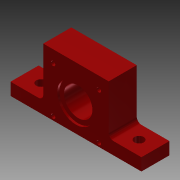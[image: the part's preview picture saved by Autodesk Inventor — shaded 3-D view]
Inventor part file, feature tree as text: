
AUTODESK INVENTOR PART (.ipt)
format: ipt  version: 2014 (Build 180170000, 170)  size: 166,400 bytes
history: native  units: in
note: dims shown in document units (in); Inventor stores cm internally (conversion verified against a paired STEP export)
features: extrude x6, sketch x6, reference x4, fillet x2, plane x1, projected_geometry x1
ambient origin geometry x8: Origin, YZ Plane, XZ Plane, XY Plane, X Axis, Y Axis, Z Axis, Center Point
bodies: Solid1 (feature_tree)
feature tree (20):
  extrude  "Extrusion1"  Depth=3.5in
  extrude  "Extrusion2"  Depth=0.75in TaperAngle=0.0deg
  fillet  "Fillet1"  Radius=0.25in
  extrude  "Extrusion3"  Depth=0.125in
  extrude  "Extrusion4"  Depth=0.06in TaperAngle=0.0deg
  sketch  "Sketch5"  dims[d16=1.75in d17=1.65in]
  plane  "Work Plane1"
  extrude  "Extrusion5"  Depth=1.65in
  extrude  "Extrusion6"  Depth=0.5in TaperAngle=0.0deg
  fillet  "Fillet2"  Radius=0.3in
  sketch  "Sketch1"  dims[d0=0.759in d1=3.5in]
  sketch  "Sketch2"  dims[d3=0.33in d6=0.75in d7=0.0in d8=0.25in]
  projected_geometry  "Projected Loop1"
  sketch  "Sketch3"  dims[d9=0.66in d10=0.0in d11=0.125in]
  sketch  "Sketch4"  dims[d12=1.0in d13=0.06in d14=0.0in]
  reference  "Reference1"
  reference  "Reference2"
  reference  "Reference3"
  reference  "Reference4"
  sketch  "Sketch6"  dims[d18=0.7095in d19=1.0in d20=0.0in d21=0.3in d22=1.0in d23=0.0in d24=1.0in d25=0.0in d26=0.5in]
